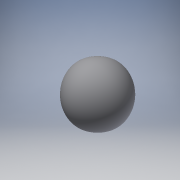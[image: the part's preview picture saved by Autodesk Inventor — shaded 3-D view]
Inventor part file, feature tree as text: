
AUTODESK INVENTOR PART (.ipt)
format: ipt  version: 2017 (Build 210142000, 142)  size: 245,248 bytes
history: native  units: in
note: dims shown in document units (in); Inventor stores cm internally (conversion verified against a paired STEP export)
features: other x1, fillet x1
ambient origin geometry x8: Origin, YZ Plane, XZ Plane, XY Plane, X Axis, Y Axis, Z Axis, Center Point
bodies: Solid1 (feature_tree), Solid2 (feature_tree)
feature tree (2):
  other  "Form1"
  fillet  "Fillet1"  [1 undecoded]
note: 1 required parameter value undecoded (feature->parameter linkage not recoverable at this tier; creation-order binding heuristic only, values carry confidence <= 0.55)
